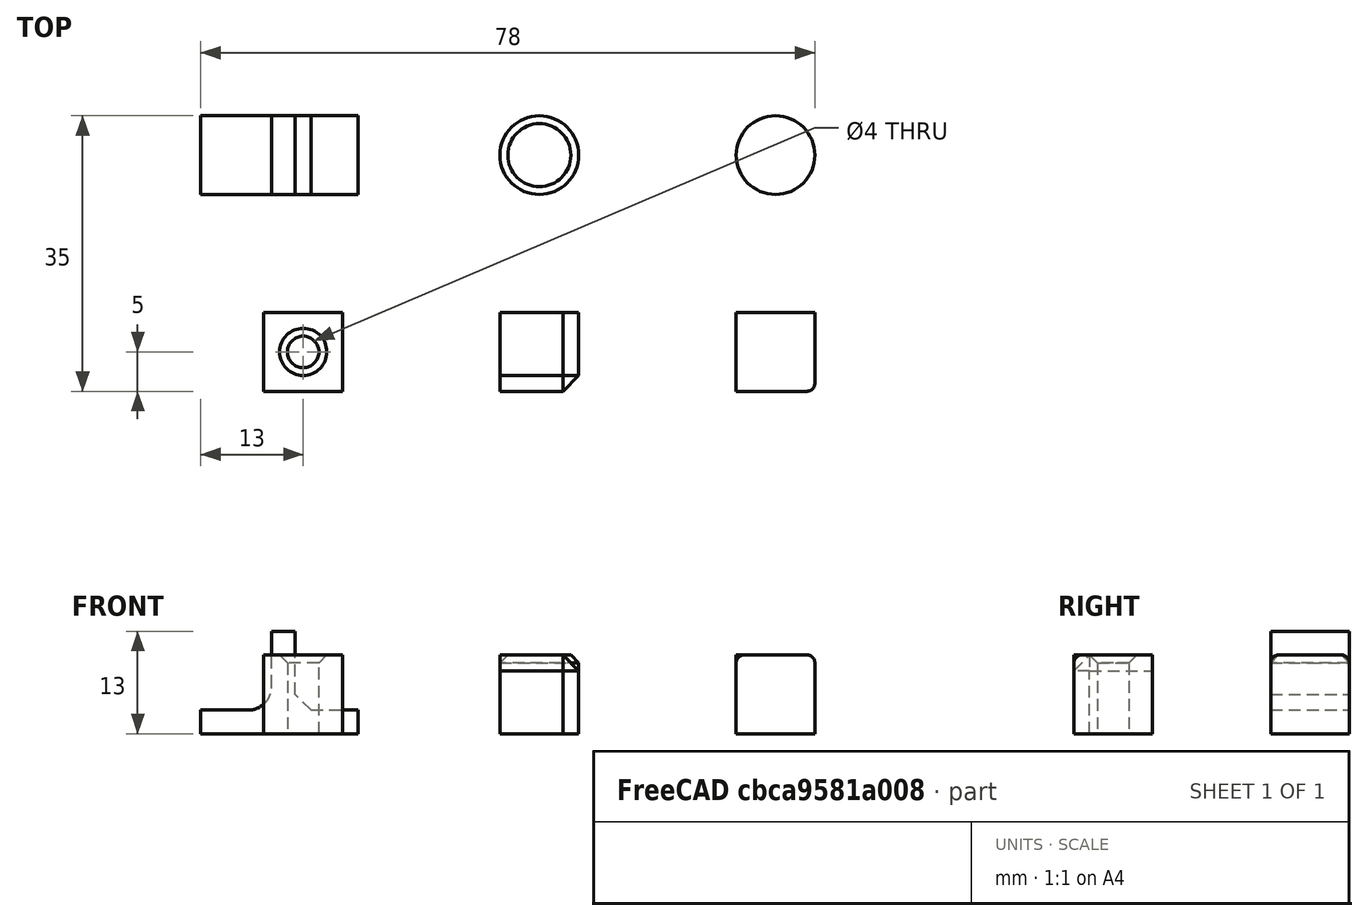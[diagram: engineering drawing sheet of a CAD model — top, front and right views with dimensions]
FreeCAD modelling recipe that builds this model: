
FCSTD DOCUMENT  (FreeCAD 1.0R39319 (Git))
Label: ojt1_t12p01_roundings_chamfers_reinforcements
License: All rights reserved
LicenseURL: https://en.wikipedia.org/wiki/All_rights_reserved
objects: Part::Box×5, Part::Chamfer×4, Part::Cylinder×3, Part::Fillet×3, Part::Cut×1, Part::MultiFuse×1
note: 17 computed .brp shape members not serialized (recipe doc carries the construction recipe); baked Part::Feature solids carry a one-line shape summary decoded from their .brp

FEATURE [Part::Box] Box  label="Cub005"
  AttacherType = Attacher::AttachEngine3D
  Height = 10
  Length = 10
  Placement = pos=(60,0,0) rot=(0,0,1;0rad)
  Width = 10
FEATURE [Part::Box] Box001  label="Cub"
  AttacherType = Attacher::AttachEngine3D
  Height = 10
  Length = 10
  Width = 10
FEATURE [Part::Box] Box002  label="Cub004"
  AttacherType = Attacher::AttachEngine3D
  Height = 10
  Length = 10
  Placement = pos=(30,0,0) rot=(0,0,1;0rad)
  Width = 10
FEATURE [Part::Cylinder] Cylinder  label="Cilindre"
  Angle = 360
  AttacherType = Attacher::AttachEngine3D
  FirstAngle = 0
  Height = 20
  Placement = pos=(5,5,-2) rot=(0,0,1;0rad)
  Radius = 2
  SecondAngle = 0
FEATURE [Part::Cut] Cut  label="Cub003"
  Base = -> Box001
  Refine = true
  Tool = -> Cylinder
FEATURE [Part::Cylinder] Cylinder001  label="Cilindre001"
  Angle = 360
  AttacherType = Attacher::AttachEngine3D
  FirstAngle = 0
  Height = 10
  Placement = pos=(65,30,0) rot=(0,0,1;0rad)
  Radius = 5
  SecondAngle = 0
FEATURE [Part::Cylinder] Cylinder002  label="Cilindre002"
  Angle = 360
  AttacherType = Attacher::AttachEngine3D
  FirstAngle = 0
  Height = 10
  Placement = pos=(35,30,0) rot=(0,0,1;0rad)
  Radius = 5
  SecondAngle = 0
FEATURE [Part::Box] Box003  label="Cub006"
  AttacherType = Attacher::AttachEngine3D
  Height = 3
  Length = 20
  Placement = pos=(-8,25,0) rot=(0,0,1;0rad)
  Width = 10
FEATURE [Part::Box] Box004  label="cub"
  AttacherType = Attacher::AttachEngine3D
  Height = 10
  Length = 3
  Placement = pos=(1,25,3) rot=(0,0,1;0rad)
  Width = 10
FEATURE [Part::MultiFuse] Fusion  label="unio"
  Refine = true
  Shapes = -> [Box003,Box004]
FEATURE [Part::Fillet] Fillet
  Base = -> Box
  EdgeLinks = -> Box [Edge5,Edge6,Edge10]
  Edges = 3 edges r=1: [Edge5,Edge6,Edge10]
FEATURE [Part::Chamfer] Chamfer
  Base = -> Box002
  EdgeLinks = -> Box002 [Edge5,Edge6,Edge10]
  Edges = 3 edges r=2: [Edge5,Edge6,Edge10]
FEATURE [Part::Chamfer] Chamfer001
  Base = -> Cut
  EdgeLinks = -> Cut [Edge10]
  Edges = 1 edges r=1: [Edge10]
FEATURE [Part::Fillet] Fillet001
  Base = -> Cylinder001
  EdgeLinks = -> Cylinder001 [Edge3]
  Edges = 1 edges r=1: [Edge3]
FEATURE [Part::Chamfer] Chamfer002
  Base = -> Cylinder002
  EdgeLinks = -> Cylinder002 [Edge3]
  Edges = 1 edges r=1: [Edge3]
FEATURE [Part::Chamfer] Chamfer003
  Base = -> Fusion
  EdgeLinks = -> Fusion [Edge16]
  Edges = 1 edges r=2: [Edge16]
FEATURE [Part::Fillet] Fillet002
  Base = -> Chamfer003
  EdgeLinks = -> Chamfer003 [Edge25]
  Edges = 1 edges r=3: [Edge25]
